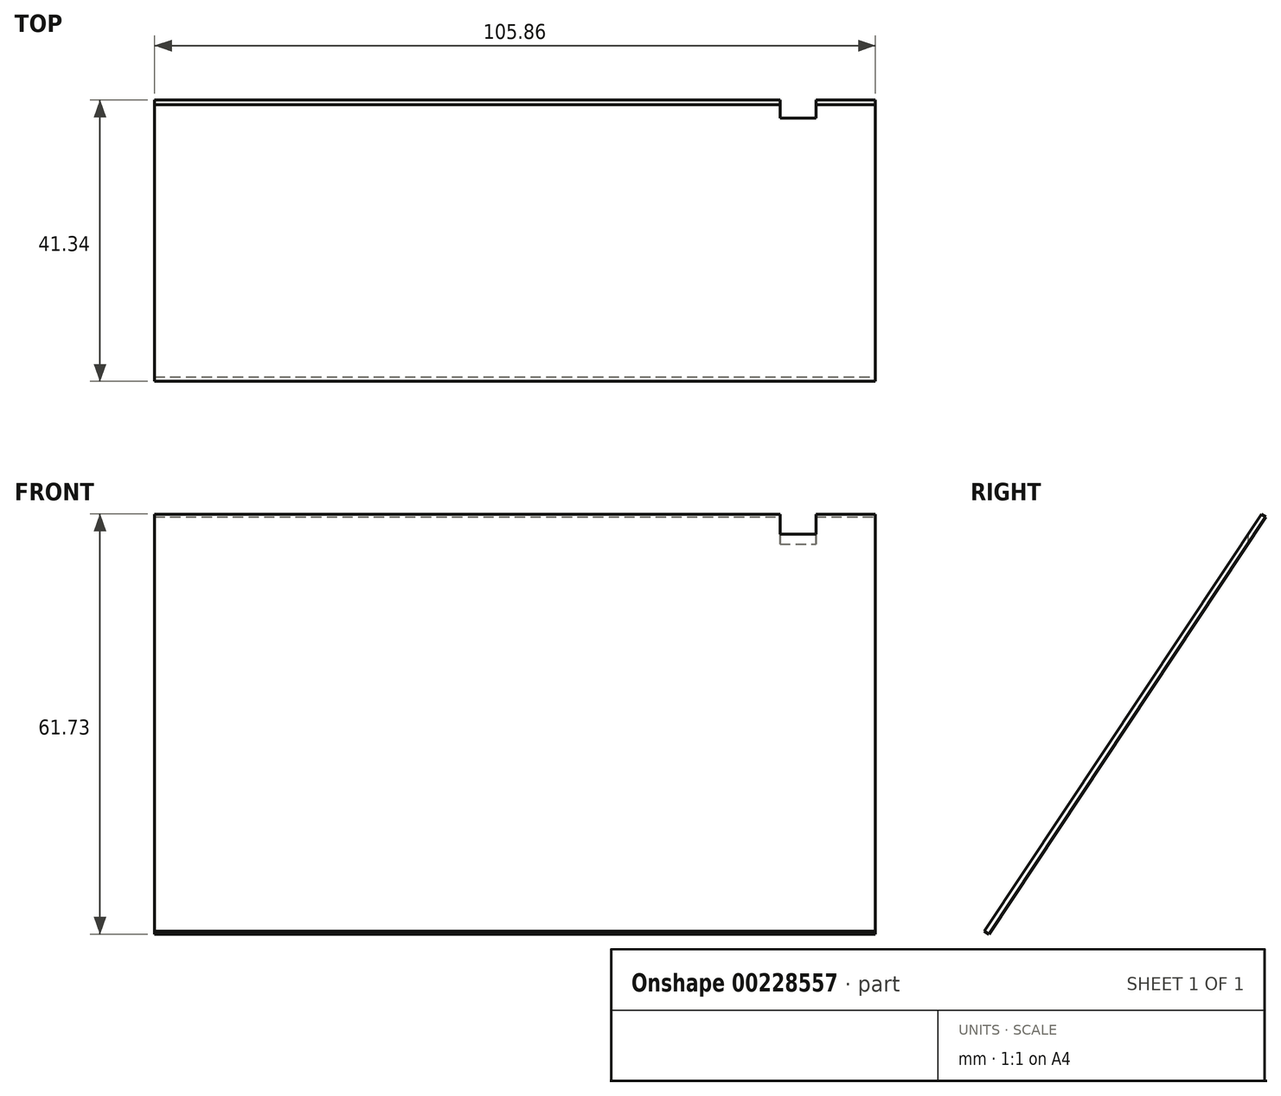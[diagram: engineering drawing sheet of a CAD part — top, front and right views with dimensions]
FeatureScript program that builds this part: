
annotation { "Feature Type Name" : "Feature", "Feature Type Description" : "" }
export const myFeature = defineFeature(function(context is Context, id is Id, definition is map)
    precondition{}
    {
        {
            var Q0;
            Q0=qCreatedBy(makeId("Right.planeOp"),FACE);
            var sketch = newSketch(context, id + "F0", { "sketchPlane" : qUnion([Q0])});
            skLineSegment(sketch, "E0", {"start": v(0, 10515.6) * mm, "end": v(-2933.7, 6096) * mm});
            skLineSegment(sketch, "E1", {"start": v(-2933.7, 6096) * mm, "end": v(-3543.3, 5177.64) * mm});
            skSolve(sketch);
        }
        {
            var Q0;
            Q0=sQuery(id+"F0.wireOp",EDGE,"E1");
            var Q1;
            Q1=sQuery(id+"F0.wireOp",EDGE,"E0");
            extrude(context, id + "F1", {"bodyType" : ToolBodyType.SURFACE, "surfaceEntities" : qUnion([Q0, Q1]), "endBound" : BoundingType.SYMMETRIC, "depth" : 9220.2 * mm});
        }
        {
            var Q0;
            Q0=makeQuery(id+"F1.opExtrude","SWEPT_FACE",FACE,{"disambiguationData":[OSD([sQuery(id+"F0.wireOp",EDGE,"E0"),sQuery(id+"F0.wireOp",EDGE,"E1")])]});
            extrude(context, id + "F2", {"entities" : qUnion([Q0]), "depth" : 69.14 * mm});
        }
        {
            var Q0;
            Q0=makeQuery(id+"F2.opExtrude","SWEPT_BODY",BODY,{"disambiguationData":[OSD([sQuery(id+"F0.wireOp",EDGE,"E0"),sQuery(id+"F0.wireOp",EDGE,"E1")])]});
            var Q1;
            Q1=makeQuery(id+"F1.opExtrude","SWEPT_BODY",BODY,{"disambiguationData":[OSD([sQuery(id+"F0.wireOp",EDGE,"E0"),sQuery(id+"F0.wireOp",EDGE,"E1")])]});
            var Q2;
            Q2=qCreatedBy(makeId("Origin.pointOp"),VERTEX);
            transform(context, id + "F3", {"entities" : qUnion([Q0, Q1]), "transformType" : TransformType.SCALE_UNIFORMLY, "scale" : 1 / 87.1, "scalePoint" : qUnion([Q2]), "makeCopy" : false});
        }
        {
            var Q0;
            {var subQ0=sQuery(id+"F0.wireOp",EDGE,"E1");var subQ1=sQuery(id+"F0.wireOp",EDGE,"E0");Q0=makeQuery(id+"F2.opExtrude","SWEPT_FACE",FACE,{"disambiguationData":[OSD([subQ1,subQ0]),TDD([makeQuery(id+"F1.opExtrude","CAP_EDGE",EDGE,{"disambiguationData":[OSD([subQ1,subQ0])],"isStart":false})])]});}
            cPlane(context, id + "F4", {"entities" : qUnion([Q0]), "cplaneType" : CPlaneType.OFFSET, "offset" : 8.75 * mm, "oppositeDirection" : true, "width" : 152.4 * mm, "height" : 152.4 * mm});
        }
        {
            var Q0;
            Q0=qCreatedBy(id+"F4.planeOp",FACE);
            var sketch = newSketch(context, id + "F5", { "sketchPlane" : qUnion([Q0])});
            skLineSegment(sketch, "E2.bottom", {"start": v(2.62, 121.17) * mm, "end": v(-2.62, 121.17) * mm});
            skLineSegment(sketch, "E2.top", {"start": v(2.62, 113.17) * mm, "end": v(-2.62, 113.17) * mm});
            skLineSegment(sketch, "E2.left", {"start": v(2.62, 121.17) * mm, "end": v(2.62, 113.17) * mm});
            skLineSegment(sketch, "E2.right", {"start": v(-2.62, 121.17) * mm, "end": v(-2.62, 113.17) * mm});
            skSolve(sketch);
        }
        {
            var Q0;
            Q0=makeQuery(id+"F5.imprint","IMPRINT",FACE,{"disambiguationData":[TD([[makeQuery(id+"F5.imprint","IMPRINT",EDGE,{"derivedFrom":sQuery(id+"F5.wireOp",EDGE,"E2.bottom")}),1.0]])]});
            extrude(context, id + "F6", {"entities" : qUnion([Q0]), "operationType" : NewBodyOperationType.REMOVE, "oppositeDirection" : true, "depth" : 5.25 * mm});
        }
    });
